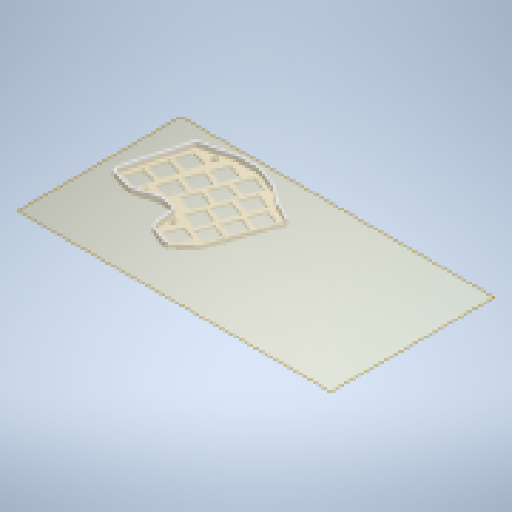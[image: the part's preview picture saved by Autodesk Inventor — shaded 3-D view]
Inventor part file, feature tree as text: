
AUTODESK INVENTOR PART (.ipt)
format: ipt  version: 2024 (Build 280153000, 153)  size: 514,560 bytes
history: native  units: mm
features: other x3, sketch x3, plane x2
ambient origin geometry x8: Origin, YZ Plane, XZ Plane, XY Plane, X Axis, Y Axis, Z Axis, Center Point
bodies: Volumenkörper1 (feature_tree)
feature tree (8):
  other  "left_top.ipt"
  other  "Volumenkörper1::left_top.ipt"
  other  "Bezeichnung1"
  sketch  "Skizze1"  dims[d0=10.0mm]
  sketch  "Skizze2"
  sketch  "Skizze3"
  plane  "Arbeitsebene1"
  plane  "Arbeitsebene2"
